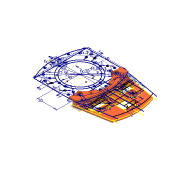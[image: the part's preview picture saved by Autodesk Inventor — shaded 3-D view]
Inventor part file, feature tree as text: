
AUTODESK INVENTOR PART (.ipt)
format: ipt  version: 2020.3 (Build 243373000, 373)  size: 276,480 bytes
history: native  units: mm
features: extrude x4, sketch x2, fillet x2, plane x1
ambient origin geometry x8: Origin, YZ Plane, XZ Plane, XY Plane, X Axis, Y Axis, Z Axis, Center Point
bodies: Solid1 (feature_tree)
feature tree (9):
  sketch  "Sketch1"  dims[d1=40.0mm d3=20.0mm d5=200.0mm d6=60.0mm d7=81.0mm d8=3.0mm d9=7.5mm d10=5.0mm d11=30.0mm d12=3.0mm d13=7.5mm d14=5.0mm d15=3.0mm d16=3.0mm d17=5.0mm d18=48.0mm d19=55.0mm d20=3.0mm d21=4.5mm d22=3.0mm d23=4.5mm d24=360.0deg d25=80.0mm d26=72.56mm d27=3.0mm d28=3.0mm d29=360.0deg d30=45.0deg d31=3.0mm d32=360.0deg d33=3.0mm d34=3.0mm d35=3.0mm d36=3.0mm d37=6.0mm]
  extrude  "Extrusion1"  Depth=6.0mm
  extrude  "Extrusion2"  Depth=15.0mm
  plane  "Work Plane1"
  sketch  "Sketch2"  dims[d38=5.0mm d39=30.0mm d40=40.5mm d41=14.0mm d42=18.0mm d43=19.0mm d44=14.0mm d45=7.0mm d46=2.0mm d47=2.0mm d48=2.0mm d49=2.0mm d50=2.0mm d51=2.0mm d52=7.0mm d53=2.5mm d54=2.5mm d55=2.0mm d56=2.0mm d57=2.5mm d58=2.0mm d59=2.0mm d60=35.0mm d61=16.0mm d62=4.0mm d63=4.0mm d64=22.0mm d65=14.0mm d66=13.962634mm d67=13.962634mm d68=2.0mm d69=4.0mm d70=2.0mm d71=0.0mm d72=4.0mm d73=0.0mm d74=1.5mm d75=2.5mm d76=0.0mm d77=2.0mm d78=6.5mm d79=6.5mm d80=1.25mm d81=0.0mm d82=15.0mm d83=0.872665mm]
  extrude  "Extrusion3"  Depth=15.0mm
  extrude  "Extrusion4"  Depth=15.0mm
  fillet  "Fillet1"  Radius=18.0mm
  fillet  "Fillet2"  Radius=19.0mm
